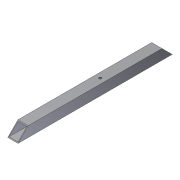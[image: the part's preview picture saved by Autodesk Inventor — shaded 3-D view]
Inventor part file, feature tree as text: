
AUTODESK INVENTOR PART (.ipt)
format: ipt  version: 2012 (Build 160160000, 160)  size: 96,256 bytes
history: native  units: in
note: dims shown in document units (in); Inventor stores cm internally (conversion verified against a paired STEP export)
features: extrude x3, sketch x3, shell x1
ambient origin geometry x8: Origin, YZ Plane, XZ Plane, XY Plane, X Axis, Y Axis, Z Axis, Center Point
bodies: Solid1 (feature_tree)
feature tree (7):
  extrude  "Extrusion1"  Depth=1.0in
  shell  "Shell1"  Thickness=15.0in
  extrude  "Extrusion2"  TaperAngle=45.0deg  [1 undecoded]
  extrude  "Extrusion3"  Depth=18.0in TaperAngle=0.0deg
  sketch  "Sketch1"  dims[d0=1.0in d1=1.0in d2=15.0in d3=0.0in]
  sketch  "Sketch2"  dims[d4=0.0625in d6=45.0deg]
  sketch  "Sketch3"  dims[d7=45.0deg d8=18.0in d9=0.0in d10=0.25in d11=0.5in d12=5.5in d13=1.0in d14=0.0in]
note: 1 required parameter value undecoded (feature->parameter linkage not recoverable at this tier; creation-order binding heuristic only, values carry confidence <= 0.55)
